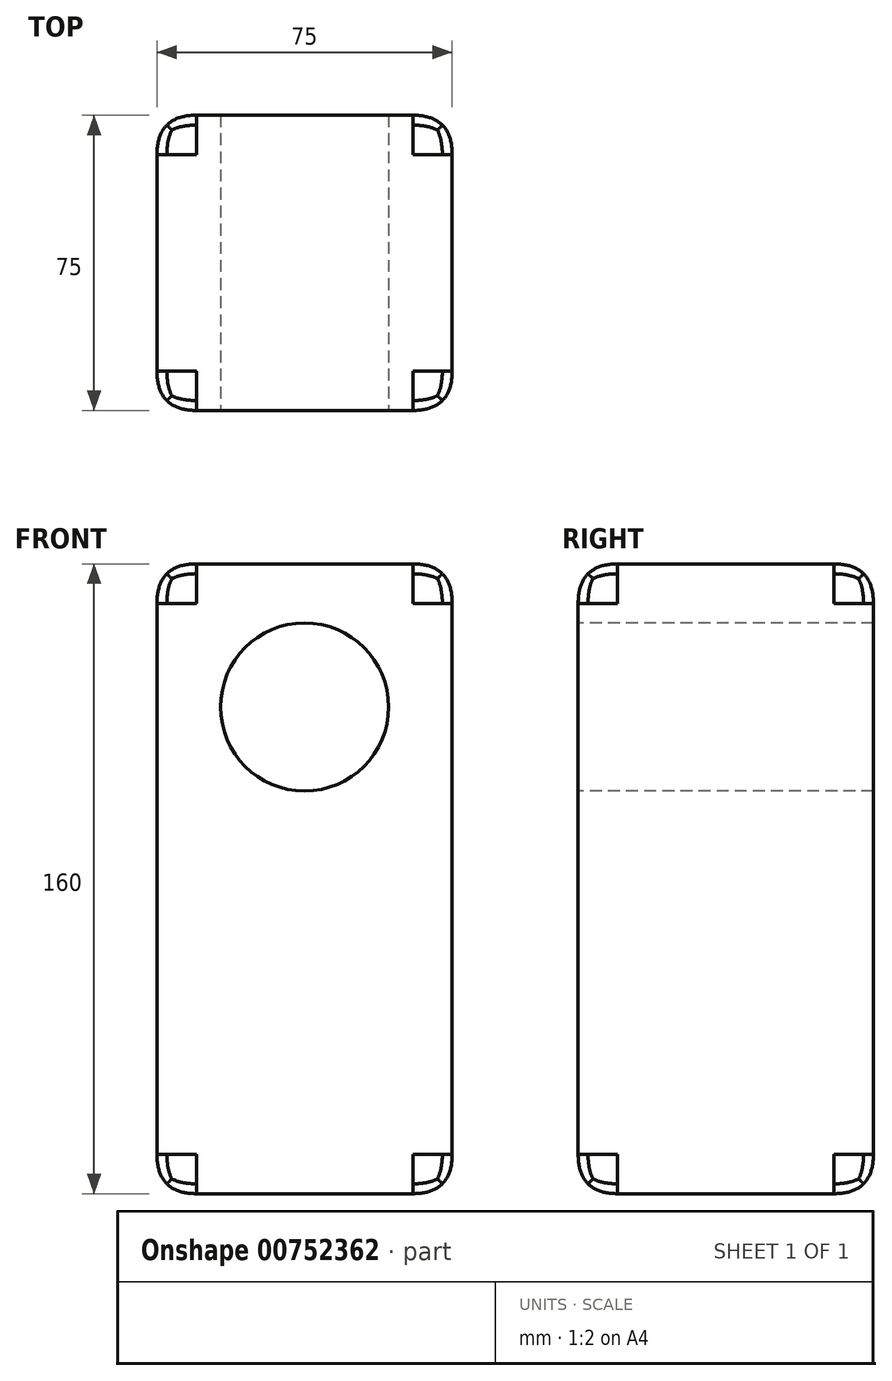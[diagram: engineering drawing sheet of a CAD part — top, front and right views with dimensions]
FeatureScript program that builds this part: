
annotation { "Feature Type Name" : "Feature", "Feature Type Description" : "" }
export const myFeature = defineFeature(function(context is Context, id is Id, definition is map)
    precondition{}
    {
        {
            var Q0;
            Q0=qCreatedBy(makeId("Front.planeOp"),FACE);
            var sketch = newSketch(context, id + "F0", { "sketchPlane" : qUnion([Q0])});
            skLineSegment(sketch, "E0.bottom", {"start": v(-37.5, 80) * mm, "end": v(37.5, 80) * mm});
            skLineSegment(sketch, "E0.top", {"start": v(-37.5, -80) * mm, "end": v(37.5, -80) * mm});
            skLineSegment(sketch, "E0.left", {"start": v(-37.5, 80) * mm, "end": v(-37.5, -80) * mm});
            skLineSegment(sketch, "E0.right", {"start": v(37.5, 80) * mm, "end": v(37.5, -80) * mm});
            skPoint(sketch, "E0.middle", {"position": v(0, 0) * mm});
            skSolve(sketch);
        }
        {
            var Q0;
            Q0=makeQuery(id+"F0.imprint","IMPRINT",FACE,{"disambiguationData":[TD([[makeQuery(id+"F0.imprint","IMPRINT",EDGE,{"derivedFrom":sQuery(id+"F0.wireOp",EDGE,"E0.bottom")}),-1.0]])]});
            extrude(context, id + "F1", {"entities" : qUnion([Q0]), "oppositeDirection" : true, "depth" : 75 * mm, "offsetDistance" : 25 * mm});
        }
        {
            var Q0;
            Q0=qCreatedBy(makeId("Front.planeOp"),FACE);
            var sketch = newSketch(context, id + "F2", { "sketchPlane" : qUnion([Q0])});
            skCircle(sketch, "E1", {"center": v(0, 43.66) * mm, "radius": 21.34 * mm});
            skSolve(sketch);
        }
        {
            var Q0;
            Q0 = qSketchRegion(id + "F2", true);
            extrude(context, id + "F3", {"entities" : qUnion([Q0]), "operationType" : NewBodyOperationType.REMOVE, "endBound" : BoundingType.UP_TO_NEXT, "oppositeDirection" : true, "depth" : 25 * mm, "offsetDistance" : 25 * mm});
        }
        {
            var Q0;
            Q0=makeQuery(id+"F1.opExtrude","SWEPT_FACE",FACE,{"disambiguationData":[OSD([sQuery(id+"F0.wireOp",EDGE,"E0.bottom")])]});
            var Q1;
            Q1=makeQuery(id+"F1.opExtrude","SWEPT_FACE",FACE,{"disambiguationData":[OSD([sQuery(id+"F0.wireOp",EDGE,"E0.right")])]});
            var Q2;
            Q2=makeQuery(id+"F1.opExtrude","SWEPT_FACE",FACE,{"disambiguationData":[OSD([sQuery(id+"F0.wireOp",EDGE,"E0.left")])]});
            var Q3;
            Q3=makeQuery(id+"F1.opExtrude","SWEPT_FACE",FACE,{"disambiguationData":[OSD([sQuery(id+"F0.wireOp",EDGE,"E0.top")])]});
            fillet(context, id + "F4", {"entities" : qUnion([Q0, Q1, Q2, Q3]), "radius" : 10 * mm, "rho" : 0.5, "crossSection" : FilletCrossSection.CONIC, "allowEdgeOverflow" : false});
        }
    });
